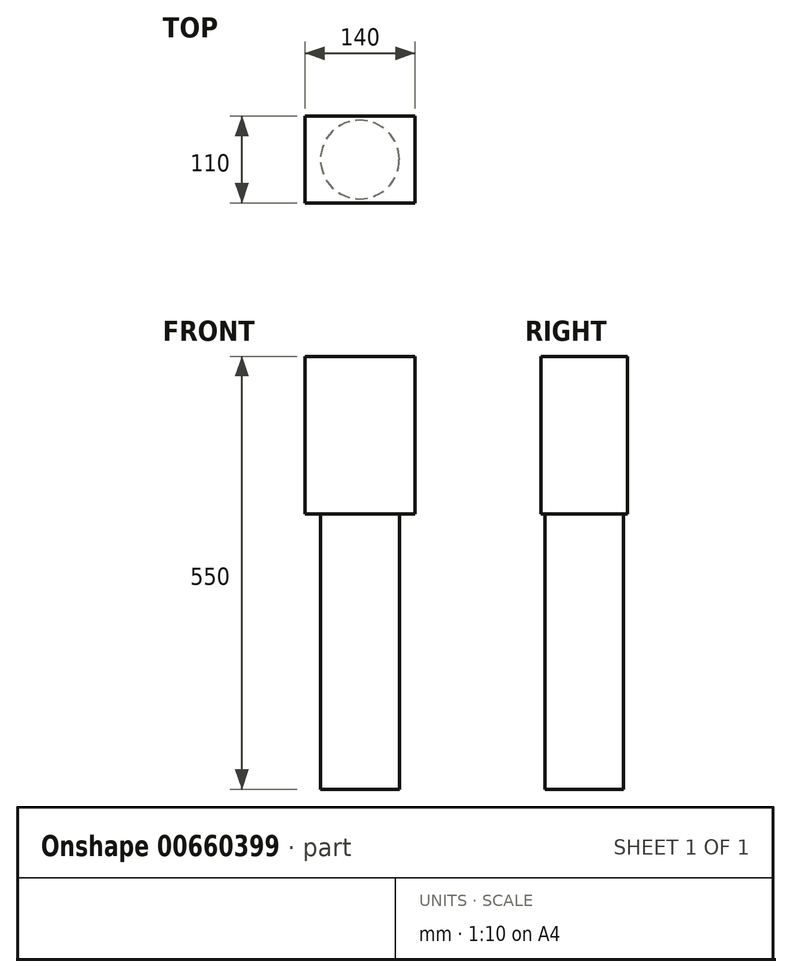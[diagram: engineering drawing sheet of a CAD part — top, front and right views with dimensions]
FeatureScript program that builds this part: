
annotation { "Feature Type Name" : "Feature", "Feature Type Description" : "" }
export const myFeature = defineFeature(function(context is Context, id is Id, definition is map)
    precondition{}
    {
        {
            var Q0;
            Q0=qCreatedBy(makeId("Top.planeOp"),FACE);
            var sketch = newSketch(context, id + "F0", { "sketchPlane" : qUnion([Q0])});
            skCircle(sketch, "E0", {"center": v(0, 0) * mm, "radius": 50 * mm});
            skSolve(sketch);
        }
        {
            var Q0;
            Q0=makeQuery(id+"F0.imprint","IMPRINT",FACE,{"disambiguationData":[TD([[makeQuery(id+"F0.imprint","IMPRINT",EDGE,{"derivedFrom":sQuery(id+"F0.wireOp",EDGE,"E0")}),1.0]])]});
            extrude(context, id + "F1", {"entities" : qUnion([Q0]), "depth" : 350 * mm, "offsetDistance" : 25 * mm});
        }
        {
            var Q0;
            Q0=makeQuery(id+"F1.opExtrude","CAP_FACE",FACE,{"disambiguationData":[OSD([sQuery(id+"F0.wireOp",EDGE,"E0")])],"isStart":false});
            var sketch = newSketch(context, id + "F2", { "sketchPlane" : qUnion([Q0])});
            skLineSegment(sketch, "E1.bottom", {"start": v(-70, 55) * mm, "end": v(70, 55) * mm});
            skLineSegment(sketch, "E1.top", {"start": v(-70, -55) * mm, "end": v(70, -55) * mm});
            skLineSegment(sketch, "E1.left", {"start": v(-70, 55) * mm, "end": v(-70, -55) * mm});
            skLineSegment(sketch, "E1.right", {"start": v(70, 55) * mm, "end": v(70, -55) * mm});
            skLineSegment(sketch, "E2", {"start": v(70, 0) * mm, "end": v(-70, 0) * mm, "construction": true});
            skLineSegment(sketch, "E3", {"start": v(0, 0) * mm, "end": v(0, -55) * mm, "construction": true});
            skSolve(sketch);
        }
        {
            var Q0;
            Q0=makeQuery(id+"F2.imprint","IMPRINT",FACE,{"disambiguationData":[TD([[makeQuery(id+"F2.imprint","IMPRINT",EDGE,{"derivedFrom":sQuery(id+"F2.wireOp",EDGE,"E1.bottom")}),-1.0]])]});
            var Q1;
            {var subQ0=sQuery(id+"F2.wireOp",EDGE,"E1.top");var subQ1=makeQuery(id+"F1.opExtrude","CAP_EDGE",EDGE,{"disambiguationData":[OSD([sQuery(id+"F0.wireOp",EDGE,"E0")])],"isStart":false});var subQ2=makeQuery(id+"F2.imprint","INTERSECT",VERTEX,{"disambiguationData":[OD(0.0)],"derivedFrom":[subQ1,subQ0]});Q1=makeQuery(id+"F2.imprint","IMPRINT",FACE,{"disambiguationData":[TD([[makeQuery(id+"F2.imprint","IMPRINT",EDGE,{"disambiguationData":[TD([[subQ2,-1.0]])],"derivedFrom":subQ0}),1.0]])]});}
            var Q2;
            Q2=makeQuery(id+"F2.imprint","IMPRINT",FACE,{"disambiguationData":[TD([[makeQuery(id+"F2.imprint","IMPRINT",EDGE,{"derivedFrom":makeQuery(id+"F1.opExtrude","CAP_EDGE",EDGE,{"disambiguationData":[OSD([sQuery(id+"F0.wireOp",EDGE,"E0")])],"isStart":false})}),1.0]])]});
            extrude(context, id + "F3", {"entities" : qUnion([Q0, Q1, Q2]), "operationType" : NewBodyOperationType.ADD, "depth" : 200 * mm, "offsetDistance" : 25 * mm});
        }
    });
